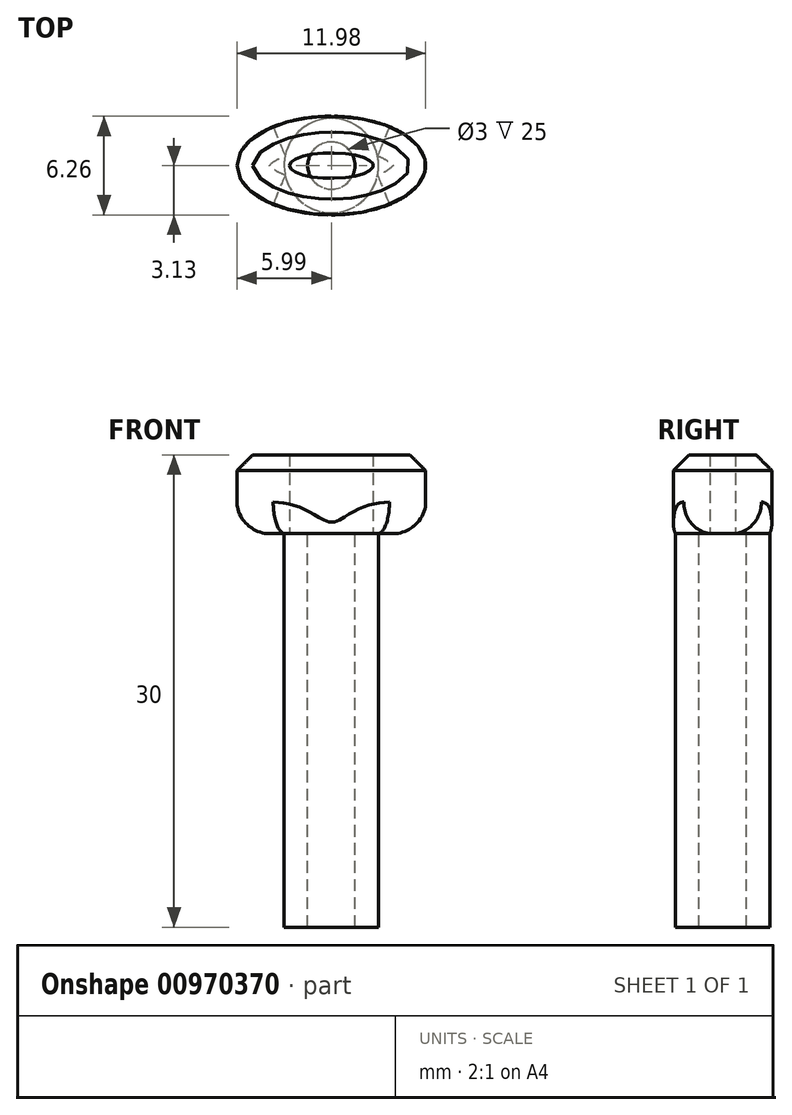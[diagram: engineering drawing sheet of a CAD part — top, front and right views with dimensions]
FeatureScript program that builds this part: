
annotation { "Feature Type Name" : "Feature", "Feature Type Description" : "" }
export const myFeature = defineFeature(function(context is Context, id is Id, definition is map)
    precondition{}
    {
        {
            var Q0;
            Q0=qCreatedBy(makeId("Front.planeOp"),FACE);
            var sketch = newSketch(context, id + "F0", { "sketchPlane" : qUnion([Q0])});
            skLineSegment(sketch, "E0", {"start": v(0, 0) * mm, "end": v(0, 25) * mm});
            skSolve(sketch);
        }
        {
            var Q0;
            Q0=qCreatedBy(makeId("Top.planeOp"),FACE);
            var sketch = newSketch(context, id + "F1", { "sketchPlane" : qUnion([Q0])});
            skCircle(sketch, "E1", {"center": v(0, 0) * mm, "radius": 3 * mm});
            skCircle(sketch, "E2", {"center": v(0, 0) * mm, "radius": 1.5 * mm});
            skSolve(sketch);
        }
        {
            var Q0;
            Q0=makeQuery(id+"F1.imprint","IMPRINT",FACE,{"disambiguationData":[TD([[makeQuery(id+"F1.imprint","IMPRINT",EDGE,{"derivedFrom":sQuery(id+"F1.wireOp",EDGE,"E1")}),1.0]])]});
            var Q1;
            Q1=sQuery(id+"F0.wireOp",EDGE,"E0");
            var Q2;
            Q2=sQuery(id+"F0.wireOp",EDGE,"f28450d4-c706-4d22-a3c8-e5cb8d2e204e");
            var Q3;
            Q3=sQuery(id+"F0.wireOp",EDGE,"7e644874-16df-472b-8ed2-20a7fe04f507");
            sweep(context, id + "F2", {"profiles" : qUnion([Q0]), "path" : qUnion([Q1, Q2, Q3])});
        }
        {
            var Q0;
            Q0=makeQuery(id+"F2.opSweep","CAP_FACE",FACE,{"disambiguationData":[OSD([sQuery(id+"F0.wireOp",VERTEX,"7e644874-16df-472b-8ed2-20a7fe04f507.end"),sQuery(id+"F1.wireOp",EDGE,"E1"),sQuery(id+"F1.wireOp",EDGE,"E2")])],"isStart":false});
            var sketch = newSketch(context, id + "F3", { "sketchPlane" : qUnion([Q0])});
            skEllipse(sketch, "E3", {"center": v(0, 0) * mm, "majorRadius": 6 * mm, "minorRadius": 3.13 * mm, "majorAxis": v(-1, 0)});
            skEllipse(sketch, "E4", {"center": v(0, 0) * mm, "majorRadius": 2.66 * mm, "minorRadius": 0.8 * mm, "majorAxis": v(-1, 0)});
            skSolve(sketch);
        }
        {
            var Q0;
            {var subQ0=sQuery(id+"F3.wireOp",EDGE,"E4");var subQ1=sQuery(id+"F0.wireOp",VERTEX,"7e644874-16df-472b-8ed2-20a7fe04f507.end");var subQ2=makeQuery(id+"F2.opSweep","CAP_EDGE",EDGE,{"disambiguationData":[OSD([subQ1,sQuery(id+"F1.wireOp",EDGE,"E2")])],"isStart":false});var subQ3=makeQuery(id+"F3.imprint","INTERSECT",VERTEX,{"disambiguationData":[OD(0.0)],"derivedFrom":[subQ2,subQ0]});Q0=makeQuery(id+"F3.imprint","IMPRINT",FACE,{"disambiguationData":[TD([[makeQuery(id+"F3.imprint","IMPRINT",EDGE,{"disambiguationData":[TD([[subQ3,1.0]])],"derivedFrom":subQ0}),-1.0]])]});}
            var Q1;
            {var subQ0=sQuery(id+"F3.wireOp",EDGE,"E4");var subQ1=sQuery(id+"F0.wireOp",VERTEX,"7e644874-16df-472b-8ed2-20a7fe04f507.end");var subQ2=makeQuery(id+"F2.opSweep","CAP_EDGE",EDGE,{"disambiguationData":[OSD([subQ1,sQuery(id+"F1.wireOp",EDGE,"E1")])],"isStart":false});var subQ3=makeQuery(id+"F3.imprint","INTERSECT",VERTEX,{"disambiguationData":[OD(2.0)],"derivedFrom":[subQ2,subQ0]});Q1=makeQuery(id+"F3.imprint","IMPRINT",FACE,{"disambiguationData":[TD([[makeQuery(id+"F3.imprint","IMPRINT",EDGE,{"disambiguationData":[TD([[subQ3,-1.0]])],"derivedFrom":subQ0}),-1.0]])]});}
            var Q2;
            Q2=makeQuery(id+"F3.imprint","IMPRINT",FACE,{"disambiguationData":[TD([[makeQuery(id+"F3.imprint","IMPRINT",EDGE,{"derivedFrom":sQuery(id+"F3.wireOp",EDGE,"E3")}),1.0]])]});
            var Q3;
            {var subQ0=sQuery(id+"F3.wireOp",EDGE,"E4");var subQ1=makeQuery(id+"F2.opSweep","CAP_EDGE",EDGE,{"disambiguationData":[OSD([sQuery(id+"F0.wireOp",VERTEX,"7e644874-16df-472b-8ed2-20a7fe04f507.end"),sQuery(id+"F1.wireOp",EDGE,"E2")])],"isStart":false});var subQ2=makeQuery(id+"F3.imprint","INTERSECT",VERTEX,{"disambiguationData":[OD(2.0)],"derivedFrom":[subQ1,subQ0]});Q3=makeQuery(id+"F3.imprint","IMPRINT",FACE,{"disambiguationData":[TD([[makeQuery(id+"F3.imprint","IMPRINT",EDGE,{"disambiguationData":[TD([[subQ2,-1.0]])],"derivedFrom":subQ0}),-1.0]])]});}
            var Q4;
            {var subQ0=sQuery(id+"F3.wireOp",EDGE,"E4");var subQ1=makeQuery(id+"F2.opSweep","CAP_EDGE",EDGE,{"disambiguationData":[OSD([sQuery(id+"F0.wireOp",VERTEX,"7e644874-16df-472b-8ed2-20a7fe04f507.end"),sQuery(id+"F1.wireOp",EDGE,"E2")])],"isStart":false});var subQ2=makeQuery(id+"F3.imprint","INTERSECT",VERTEX,{"disambiguationData":[OD(0.0)],"derivedFrom":[subQ1,subQ0]});Q4=makeQuery(id+"F3.imprint","IMPRINT",FACE,{"disambiguationData":[TD([[makeQuery(id+"F3.imprint","IMPRINT",EDGE,{"disambiguationData":[TD([[subQ2,-1.0]])],"derivedFrom":subQ0}),-1.0]])]});}
            extrude(context, id + "F4", {"entities" : qUnion([Q0, Q1, Q2, Q3, Q4]), "operationType" : NewBodyOperationType.ADD, "depth" : 5 * mm, "offsetDistance" : 25 * mm});
        }
        {
            var Q0;
            Q0=makeQuery(id+"F4.opExtrude","CAP_EDGE",EDGE,{"disambiguationData":[OSD([sQuery(id+"F3.wireOp",EDGE,"E3")])],"isStart":true});
            fillet(context, id + "F5", {"entities" : qUnion([Q0]), "radius" : 2 * mm, "tangentPropagation" : true, "allowEdgeOverflow" : false});
        }
        {
            var Q0;
            Q0=makeQuery(id+"F4.opExtrude","CAP_EDGE",EDGE,{"disambiguationData":[OSD([sQuery(id+"F3.wireOp",EDGE,"E3")])],"isStart":false});
            chamfer(context, id + "F6", {"entities" : qUnion([Q0]), "width" : 1 * mm, "tangentPropagation" : true});
        }
    });
